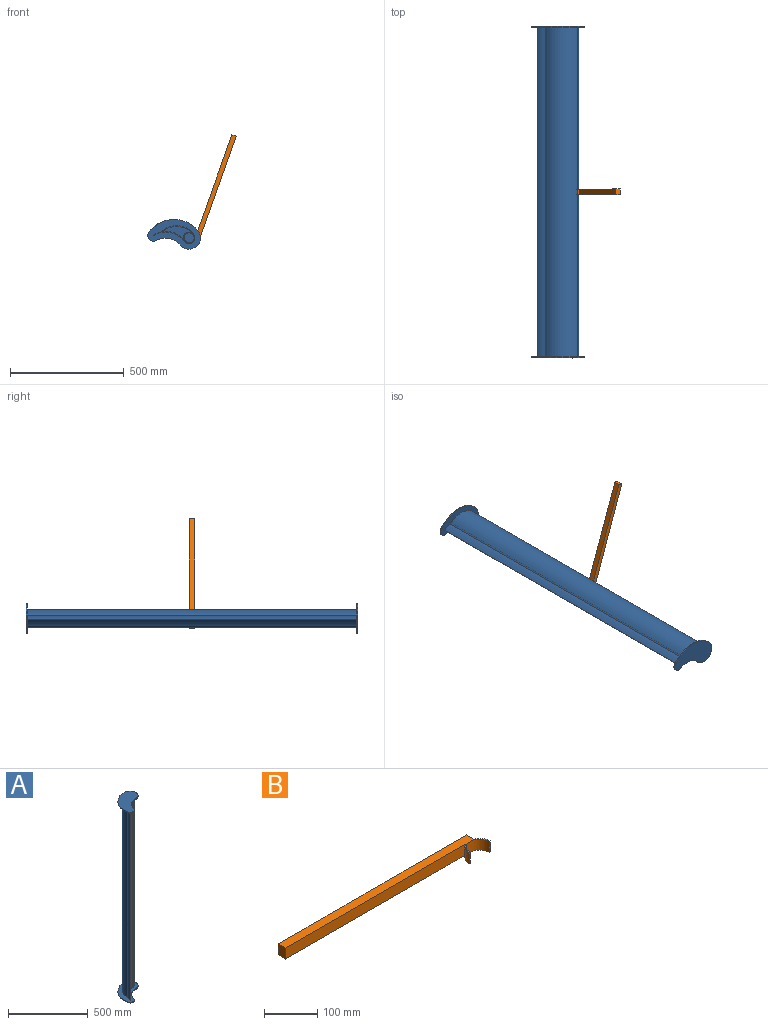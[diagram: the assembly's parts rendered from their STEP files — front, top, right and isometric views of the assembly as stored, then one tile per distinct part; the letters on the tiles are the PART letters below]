
ASSEMBLY  parts=2 mates=1
PART A: 27 faces, bbox 186.8x187.7x1460 mm
  f0: cylinder r=25mm len=1450mm, axis (0,0,-1), area 113939.2mm2, adj f1,f6,f12,f18
  f1: plane 1450x2.5mm, normal (1,0,0), area 3625mm2, adj f0,f2,f12,f18
  f2: cylinder r=100mm len=1450mm, axis (0,0,-1), area 234624.9mm2, adj f1,f3,f12,f18
  f3: cylinder r=100mm len=1450mm, axis (0,0,-1), area 53859.5mm2, adj f2,f4,f12,f18
  f4: plane 1450x2.98mm, normal (-0.11,-0.99,0), area 4350mm2, adj f3,f5,f12,f18
  f5: cylinder r=97mm len=1450mm, axis (0,0,-1), area 220932.5mm2, adj f4,f6,f12,f18
  f6: plane 1450x2.64mm, normal (0.99,-0.11,0), area 3858.8mm2, adj f0,f5,f12,f18
  f7: cylinder r=88.03mm len=84.35mm, axis (0,0,-1), area 563.7mm2, adj f8,f10,f11,f12
  f8: cylinder r=50mm len=100mm, axis (0,0,-1), area 785.4mm2, adj f7,f9,f11,f12
  f9: cylinder r=136.78mm len=162.5mm, axis (0,0,-1), area 1203.7mm2, adj f8,f10,f11,f12
  f10: cylinder r=25mm len=50mm, axis (0,0,-1), area 392.7mm2, adj f7,f9,f11,f12
  f11: plane 187.67x186.79mm, normal (0,0,1), area 19238.2mm2, adj f7,f8,f9,f10
  f12: plane 187.67x186.79mm, normal (0,0,-1), area 13428.7mm2, adj f0,f1,f2,f3,f4,f5,f6,f7
  f13: cylinder r=88.03mm len=84.35mm, axis (0,0,1), area 563.7mm2, adj f14,f16,f17,f18
  f14: cylinder r=25mm len=50mm, axis (0,0,1), area 391mm2, adj f13,f15,f17,f18
  f15: cylinder r=136.84mm len=162.85mm, axis (0,0,1), area 1205.6mm2, adj f14,f16,f17,f18
  f16: cylinder r=50mm len=100mm, axis (0,0,1), area 785.4mm2, adj f13,f15,f17,f18
  f17: plane 187.67x186.84mm, normal (0,0,-1), area 19244.1mm2, adj f13,f14,f15,f16
  f18: plane 187.67x186.84mm, normal (0,0,1), area 13434.5mm2, adj f0,f1,f2,f3,f4,f5,f6,f13
  f19: plane 96.47x91.25mm, normal (0,0,-1), area 2915.5mm2, adj f20,f21,f22
  f20: cylinder r=25mm len=1450mm, axis (0,0,-1), area 95829.6mm2, adj f19,f21,f22,f23
  f21: cylinder r=100mm len=1450mm, axis (0,0,-1), area 155856.6mm2, adj f19,f20,f22,f23
  f22: cylinder r=97mm len=1450mm, axis (0,0,-1), area 212059.6mm2, adj f19,f20,f21,f23
  f23: plane 96.47x91.25mm, normal (0,0,1), area 2915.5mm2, adj f20,f21,f22
  f24: plane 44x44mm, normal (0,0,1), area 1520.5mm2, adj f26
  f25: plane 44x44mm, normal (0,0,-1), area 1520.5mm2, adj f26
  f26: cylinder r=22mm len=1450mm, axis (0,0,-1), area 200433.6mm2, adj f24,f25
PART B: 11 faces, bbox 517.5x45x25 mm
  f0: plane 25x20mm, normal (-1,0,0), area 500mm2, adj f1,f8,f9,f10
  f1: plane 478.54x25mm, normal (0,-1,0), area 11963.6mm2, adj f0,f2,f9,f10
  f2: cylinder r=27.5mm len=25mm, axis (0,0,-1), area 784.5mm2, adj f1,f3,f9,f10
  f3: plane 25x2.5mm, normal (0,-1,0), area 62.5mm2, adj f2,f4,f9,f10
  f4: cylinder r=25mm len=50mm, axis (0,0,-1), area 1963.5mm2, adj f3,f5,f9,f10
  f5: plane 25x2.5mm, normal (0,-1,0), area 62.5mm2, adj f4,f6,f9,f10
  f6: cylinder r=27.5mm len=25.62mm, axis (0,0,-1), area 824.1mm2, adj f5,f7,f9,f10
  f7: plane 25x19.38mm, normal (1,0,0), area 484.6mm2, adj f6,f8,f9,f10
  f8: plane 500x25mm, normal (0,1,0), area 12500mm2, adj f0,f7,f9,f10
  f9: plane 517.5x45mm, normal (0,0,1), area 10168.1mm2, adj f0,f1,f2,f3,f4,f5,f6,f7
  f10: plane 517.5x45mm, normal (0,0,-1), area 10168.1mm2, adj f0,f1,f2,f3,f4,f5,f6,f7
PLACE A rot(axis=(0.84,0.39,-0.39),100.2deg) t=(-35,725,490)mm
PLACE B rot(axis=(0.45,0.63,-0.63),131.9deg) t=(153.33,12.5,943.05)mm
MATE revolute B.f2 <-> A.f0  axis (0,1,0) through (-35,0,490)mm
